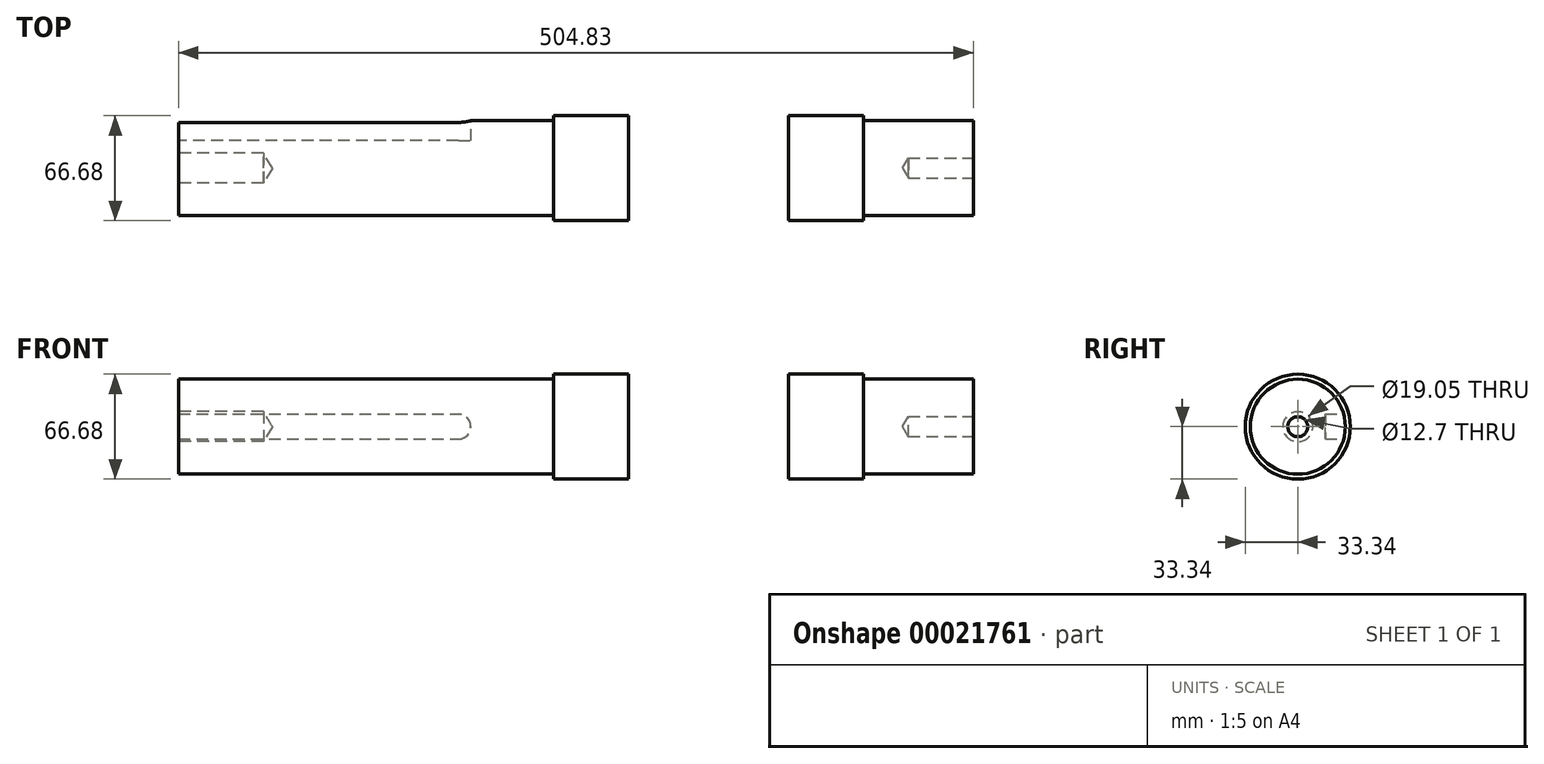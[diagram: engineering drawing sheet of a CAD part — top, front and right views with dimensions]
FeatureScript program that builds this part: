
annotation { "Feature Type Name" : "Feature", "Feature Type Description" : "" }
export const myFeature = defineFeature(function(context is Context, id is Id, definition is map)
    precondition{}
    {
        {
            var Q0;
            Q0=qCreatedBy(makeId("Front.planeOp"),FACE);
            var sketch = newSketch(context, id + "F0", { "sketchPlane" : qUnion([Q0])});
            skLineSegment(sketch, "E0", {"start": v(0, 0) * mm, "end": v(-50.8, 0) * mm, "construction": true});
            skLineSegment(sketch, "E1", {"start": v(0, 0) * mm, "end": v(50.8, 0) * mm, "construction": true});
            skLineSegment(sketch, "E2.bottom", {"start": v(-50.8, 0) * mm, "end": v(-98.43, 0) * mm});
            skLineSegment(sketch, "E2.top", {"start": v(-50.8, 33.34) * mm, "end": v(-98.43, 33.34) * mm});
            skLineSegment(sketch, "E2.left", {"start": v(-50.8, 0) * mm, "end": v(-50.8, 33.34) * mm});
            skLineSegment(sketch, "E2.right", {"start": v(-98.43, 0) * mm, "end": v(-98.43, 33.34) * mm});
            skLineSegment(sketch, "E3.bottom", {"start": v(-98.43, 0) * mm, "end": v(-336.55, 0) * mm});
            skLineSegment(sketch, "E3.top", {"start": v(-98.43, 30.16) * mm, "end": v(-336.55, 30.16) * mm});
            skLineSegment(sketch, "E3.left", {"start": v(-98.43, 0) * mm, "end": v(-98.43, 30.16) * mm});
            skLineSegment(sketch, "E3.right", {"start": v(-336.55, 0) * mm, "end": v(-336.55, 30.16) * mm});
            skLineSegment(sketch, "E4.bottom", {"start": v(50.8, 0) * mm, "end": v(98.42, 0) * mm});
            skLineSegment(sketch, "E4.top", {"start": v(50.8, 33.34) * mm, "end": v(98.42, 33.34) * mm});
            skLineSegment(sketch, "E4.left", {"start": v(50.8, 0) * mm, "end": v(50.8, 33.34) * mm});
            skLineSegment(sketch, "E4.right", {"start": v(98.42, 0) * mm, "end": v(98.42, 33.34) * mm});
            skLineSegment(sketch, "E5.bottom", {"start": v(98.42, 0) * mm, "end": v(168.28, 0) * mm});
            skLineSegment(sketch, "E5.top", {"start": v(98.42, 30.16) * mm, "end": v(168.28, 30.16) * mm});
            skLineSegment(sketch, "E5.left", {"start": v(98.42, 0) * mm, "end": v(98.42, 30.16) * mm});
            skLineSegment(sketch, "E5.right", {"start": v(168.28, 0) * mm, "end": v(168.28, 30.16) * mm});
            skSolve(sketch);
        }
        {
            var Q0;
            Q0=makeQuery(id+"F0.imprint","IMPRINT",FACE,{"disambiguationData":[TD([[makeQuery(id+"F0.imprint","IMPRINT",EDGE,{"derivedFrom":sQuery(id+"F0.wireOp",EDGE,"E3.bottom")}),-1.0]])]});
            var Q1;
            Q1=makeQuery(id+"F0.imprint","IMPRINT",FACE,{"disambiguationData":[TD([[makeQuery(id+"F0.imprint","IMPRINT",EDGE,{"derivedFrom":sQuery(id+"F0.wireOp",EDGE,"E2.bottom")}),-1.0]])]});
            var Q2;
            Q2=makeQuery(id+"F0.imprint","IMPRINT",FACE,{"disambiguationData":[TD([[makeQuery(id+"F0.imprint","IMPRINT",EDGE,{"derivedFrom":sQuery(id+"F0.wireOp",EDGE,"E4.bottom")}),1.0]])]});
            var Q3;
            Q3=makeQuery(id+"F0.imprint","IMPRINT",FACE,{"disambiguationData":[TD([[makeQuery(id+"F0.imprint","IMPRINT",EDGE,{"derivedFrom":sQuery(id+"F0.wireOp",EDGE,"E5.bottom")}),1.0]])]});
            var Q4;
            Q4=sQuery(id+"F0.wireOp",EDGE,"E0");
            revolve(context, id + "F1", {"entities" : qUnion([Q0, Q1, Q2, Q3]), "axis" : qUnion([Q4]), "revolveType" : RevolveType.FULL});
        }
        {
            var Q0;
            Q0=qCreatedBy(makeId("Front.planeOp"),FACE);
            cPlane(context, id + "F2", {"entities" : qUnion([Q0]), "cplaneType" : CPlaneType.OFFSET, "offset" : 30.16 * mm, "oppositeDirection" : true, "width" : 152.4 * mm, "height" : 152.4 * mm});
        }
        {
            var Q0;
            Q0=qCreatedBy(id+"F2.planeOp",FACE);
            var sketch = newSketch(context, id + "F3", { "sketchPlane" : qUnion([Q0])});
            skArc(sketch, "E6", {"start": v(-158.75, -7.94) * mm, "mid": v(-150.81, 0) * mm, "end": v(-158.75, 7.94) * mm});
            skLineSegment(sketch, "E7", {"start": v(-158.75, 7.94) * mm, "end": v(-349.25, 7.94) * mm});
            skLineSegment(sketch, "E8", {"start": v(-349.25, 7.94) * mm, "end": v(-349.25, -7.94) * mm});
            skLineSegment(sketch, "E9", {"start": v(-158.75, -7.94) * mm, "end": v(-349.25, -7.94) * mm});
            skSolve(sketch);
        }
        {
            var Q0;
            Q0=makeQuery(id+"F3.imprint","IMPRINT",FACE,{"disambiguationData":[TD([[makeQuery(id+"F3.imprint","IMPRINT",EDGE,{"derivedFrom":sQuery(id+"F3.wireOp",EDGE,"b6236cba-a9f8-42f8-8c92-b6982e75b4f1")}),1.0]])]});
            var Q1;
            Q1=makeQuery(id+"F3.imprint","IMPRINT",FACE,{"disambiguationData":[TD([[makeQuery(id+"F3.imprint","IMPRINT",EDGE,{"derivedFrom":sQuery(id+"F3.wireOp",EDGE,"E6")}),1.0]])]});
            extrude(context, id + "F4", {"entities" : qUnion([Q0, Q1]), "operationType" : NewBodyOperationType.REMOVE, "depth" : 12.7 * mm});
        }
        {
            var Q0;
            Q0=makeQuery(id+"F1.opRevolve","SWEPT_FACE",FACE,{"disambiguationData":[OSD([sQuery(id+"F0.wireOp",EDGE,"E5.right")])]});
            var sketch = newSketch(context, id + "F5", { "sketchPlane" : qUnion([Q0])});
            skPoint(sketch, "E10", {"position": v(0, 0) * mm});
            skSolve(sketch);
        }
        {
            var Q0;
            Q0=sQuery(id+"F5.wireOp",VERTEX,"E10");
            var Q1;
            Q1=makeQuery(id+"F1.opRevolve","SWEPT_BODY",BODY,{"disambiguationData":[OSD([sQuery(id+"F0.wireOp",EDGE,"E4.bottom"),sQuery(id+"F0.wireOp",EDGE,"E4.top"),sQuery(id+"F0.wireOp",EDGE,"E4.left"),sQuery(id+"F0.wireOp",EDGE,"E4.right"),sQuery(id+"F0.wireOp",EDGE,"E5.bottom"),sQuery(id+"F0.wireOp",EDGE,"E5.top"),sQuery(id+"F0.wireOp",EDGE,"E5.right")])]});
            hole(context, id + "F6", {"style" : HoleStyle.SIMPLE, "holeDiameter" : 12.7 * mm, "endStyle" : HoleEndStyle.BLIND, "holeDepth" : 41.27 * mm, "locations" : qUnion([Q0]), "scope" : qUnion([Q1])});
        }
        {
            var Q0;
            Q0=makeQuery(id+"F1.opRevolve","SWEPT_FACE",FACE,{"disambiguationData":[OSD([sQuery(id+"F0.wireOp",EDGE,"E3.right")])]});
            var sketch = newSketch(context, id + "F7", { "sketchPlane" : qUnion([Q0])});
            skPoint(sketch, "E11", {"position": v(0, 0) * mm});
            skSolve(sketch);
        }
        {
            var Q0;
            Q0=sQuery(id+"F7.wireOp",VERTEX,"E11");
            var Q1;
            Q1=makeQuery(id+"F1.opRevolve","SWEPT_BODY",BODY,{"disambiguationData":[OSD([sQuery(id+"F0.wireOp",EDGE,"E2.bottom"),sQuery(id+"F0.wireOp",EDGE,"E2.top"),sQuery(id+"F0.wireOp",EDGE,"E2.left"),sQuery(id+"F0.wireOp",EDGE,"E2.right"),sQuery(id+"F0.wireOp",EDGE,"E3.bottom"),sQuery(id+"F0.wireOp",EDGE,"E3.top"),sQuery(id+"F0.wireOp",EDGE,"E3.right")])]});
            hole(context, id + "F8", {"style" : HoleStyle.SIMPLE, "holeDiameter" : 19.05 * mm, "endStyle" : HoleEndStyle.BLIND, "holeDepth" : 53.97 * mm, "locations" : qUnion([Q0]), "scope" : qUnion([Q1])});
        }
    });
